# Revit family: Electrical_Equipment-Floor_Box-Hubbell_Wiring-Multi_Service_Flush_Cover-PFB1
name_source: partatom
category: Electrical Fixtures
revit_build: Autodesk Revit 2015 (Build: 20140606_1530(x64)
units: mm (PartAtom-declared; Revit-internal decimal feet)

## types (5) — shared parameters
Adapter Ring Part Number = PFBA1A
Assembly Code = D5020115
Can Material = Non_Metallic-Hubbell-Plastic
Conduit Connector 1 Radius = 0' - 0 1/2"
Conduit Connector 2 Radius = 0' - 0 3/8"
Conduit Connector_1 Description = Conduit 1in. Connection
Conduit Connector_2 Description = Conduit 1in. Connection
Conduit Connector_3 Description = Conduit 0.75in. Connection
Conduit Connector_4 Description = Conduit 0.75in. Connection
Conduit Connector_5 Description = Y-Adapter 0.75in. Connection
Conduit Connector_6 Description = Y-Adapter 0.75in. Connection
Conduit Connector_7 Description = Y-Adapter 0.75in. Connection
Conduit Connector_8 Description = Y-Adapter 0.75in. Connection
Default Elevation = 0' - 0"
Description = Flush Round Multi-Service Floor Box
Low Voltage Divider Part Number = PFBT1A
Manufacturer = Hubbell-Wiring
Model = PFB1
Product Documentation Link = http://ecatalog.hubbell-wiring.com
Product Page URL = http://ecatalog.hubbell-wiring.com
Product data url = https://bimobject.com
URL = http://www.hubbell-wiring.com
Y-Adapter Part Number = PFBYA1

## per-type parameters (varying)
| type | Cover Material |
| PFBCBRA - Brown Non-Metallic | Non_Metallic-Hubbell-Brown |
| PFBCIA - Ivory Non-Metallic | Non_Metallic-Hubbell-Ivory |
| PFBCGYA - Gray Non-Metallic | Non_Metallic-Hubbell-Gray |
| SF39253A - Brass | Metal-Hubbell-Brass |
| PFBCBLA - Black Non-Metallic | Non_Metallic-Hubbell-Black |

## geometry (parser evidence)
native form markers: Blend x54, Sweep x16
no freeform markers — native parametric forms only
